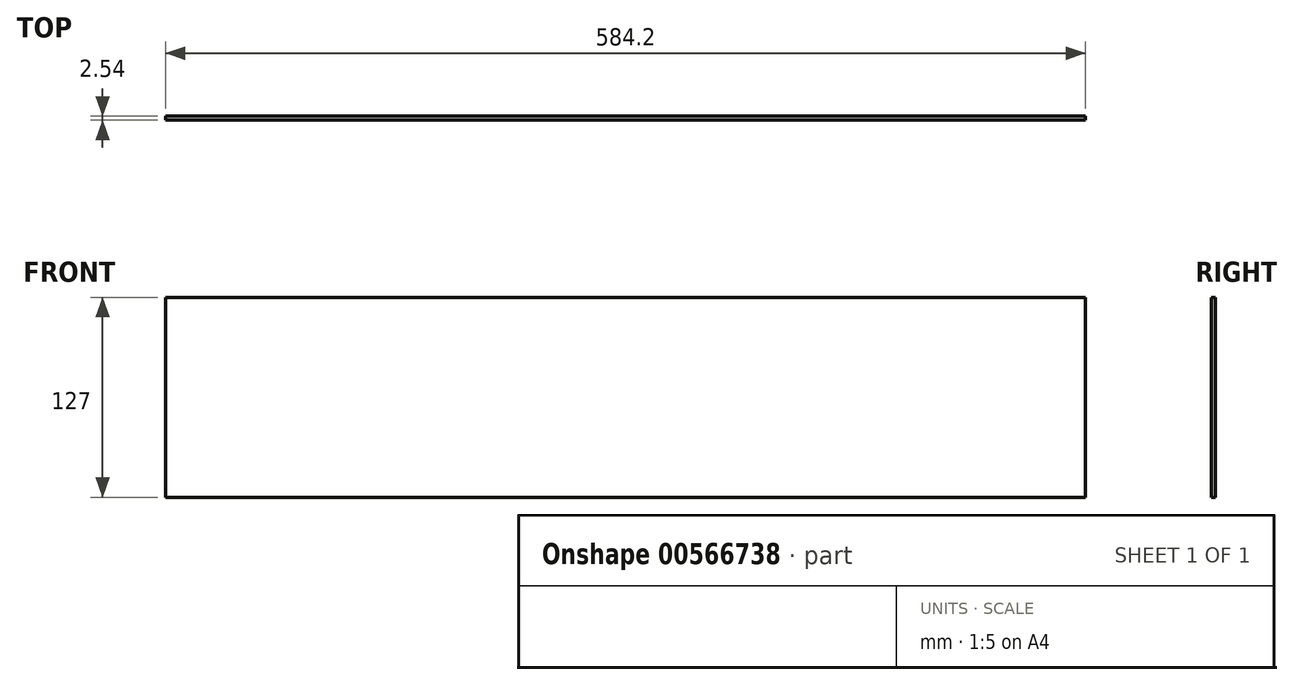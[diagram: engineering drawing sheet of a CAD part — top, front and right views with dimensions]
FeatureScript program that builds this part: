
annotation { "Feature Type Name" : "Feature", "Feature Type Description" : "" }
export const myFeature = defineFeature(function(context is Context, id is Id, definition is map)
    precondition{}
    {
        {
            var Q0;
            Q0=qCreatedBy(makeId("Front.planeOp"),FACE);
            var sketch = newSketch(context, id + "F0", { "sketchPlane" : qUnion([Q0])});
            skLineSegment(sketch, "E0.bottom", {"start": v(292.1, -63.5) * mm, "end": v(-292.1, -63.5) * mm});
            skLineSegment(sketch, "E0.top", {"start": v(292.1, 63.5) * mm, "end": v(-292.1, 63.5) * mm});
            skLineSegment(sketch, "E0.left", {"start": v(292.1, -63.5) * mm, "end": v(292.1, 63.5) * mm});
            skLineSegment(sketch, "E0.right", {"start": v(-292.1, -63.5) * mm, "end": v(-292.1, 63.5) * mm});
            skPoint(sketch, "E0.middle", {"position": v(0, 0) * mm});
            skSolve(sketch);
        }
        {
            var Q0;
            Q0 = qSketchRegion(id + "F0", true);
            extrude(context, id + "F1", {"entities" : qUnion([Q0]), "endBound" : BoundingType.SYMMETRIC, "depth" : 2.54 * mm, "offsetDistance" : 25.4 * mm});
        }
    });
